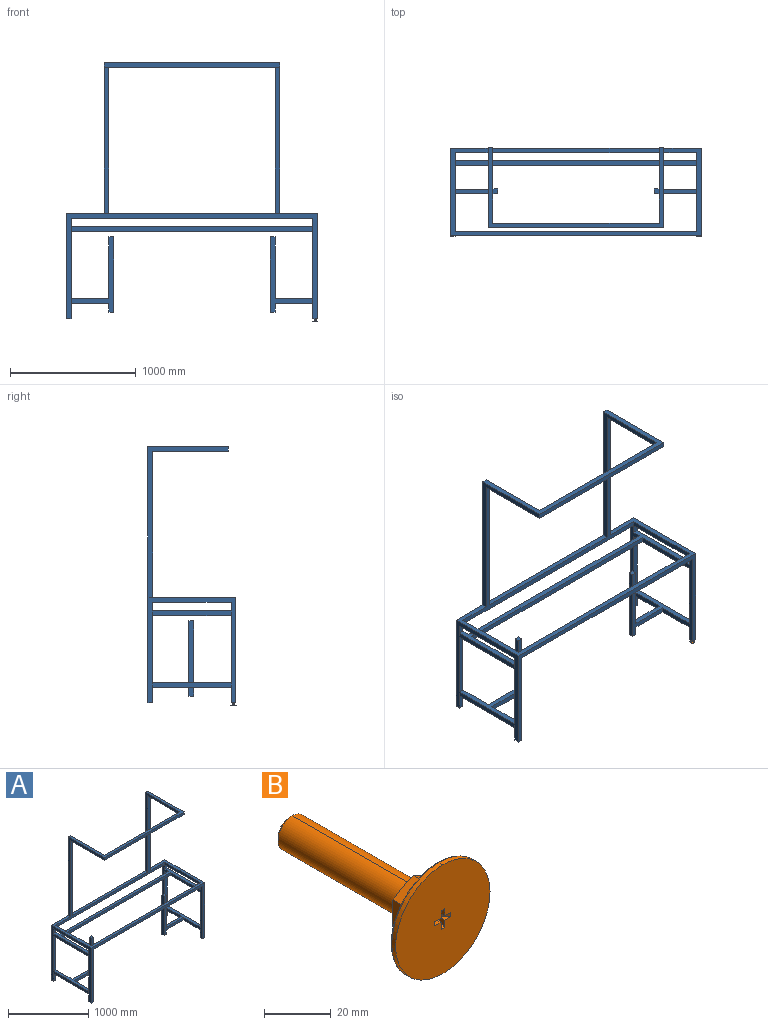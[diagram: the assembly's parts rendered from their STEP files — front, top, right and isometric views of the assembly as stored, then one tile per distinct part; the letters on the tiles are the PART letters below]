
ASSEMBLY  parts=2 mates=1
PART A: 72 faces, bbox 2000.2x700x2038.1 mm
  f0: plane 1200x600mm, normal (1,0,0), area 67128.4mm2, adj f2,f4,f19,f65,f67,f69
  f1: plane 1200x600mm, normal (-1,0,0), area 67128.4mm2, adj f2,f4,f19,f65,f67,f69
  f2: plane 1923.8x1200mm, normal (0,-1,0), area 161833.6mm2, adj f0,f1,f3,f4,f15,f21,f22,f64
  f3: plane 2000x700mm, normal (0,0,1), area 146593.6mm2, adj f2,f17,f18,f19,f20,f21,f22,f23
  f4: plane 1323.8x38.1mm, normal (0,0,1), area 50436.8mm2, adj f0,f1,f2,f19
  f5: plane 298.39x38.1mm, normal (1,0,0), area 11368.6mm2, adj f7,f51,f53,f57
  f6: plane 523.8x38.1mm, normal (1,0,0), area 19956.8mm2, adj f7,f34,f35,f39
  f7: plane 800x38.1mm, normal (0,1,0), area 27592mm2, adj f5,f6,f16,f23,f25,f26,f34,f35
  f8: plane 800x38.1mm, normal (0,-1,0), area 27592mm2, adj f16,f23,f27,f28,f34,f35,f49,f51
  f9: plane 800x325.41mm, normal (-1,0,0), area 43784.9mm2, adj f10,f12,f15,f19,f29,f31,f34,f35
  f10: plane 533.8x38.1mm, normal (0,-1,0), area 20337.8mm2, adj f9,f18,f35,f36
  f11: plane 533.8x38.1mm, normal (0,1,0), area 20337.8mm2, adj f18,f30,f35,f36
  f12: plane 70x38.1mm, normal (0,-1,0), area 2667mm2, adj f9,f14,f18,f34
  f13: plane 70x38.1mm, normal (0,1,0), area 2667mm2, adj f14,f18,f30,f34
  f14: plane 623.8x38.1mm, normal (0,0,-1), area 23766.8mm2, adj f12,f13,f18,f22
  f15: plane 1923.8x38.1mm, normal (0,0,-1), area 73296.8mm2, adj f2,f9,f19,f27
  f16: plane 623.8x38.1mm, normal (0,0,-1), area 23766.8mm2, adj f7,f8,f21,f23
  f17: plane 2000x838.1mm, normal (0,-1,0), area 137160mm2, adj f3,f18,f23,f24,f25,f26,f30,f33
  f18: plane 838.1x700mm, normal (1,0,0), area 135163.6mm2, adj f3,f10,f11,f12,f13,f14,f17,f19
  f19: plane 2038.1x2000mm, normal (0,1,0), area 228600mm2, adj f0,f1,f3,f4,f9,f15,f18,f23
  f20: plane 1923.8x38.1mm, normal (0,1,0), area 73296.8mm2, adj f3,f21,f22,f24
  f21: plane 623.8x38.1mm, normal (1,0,0), area 23766.8mm2, adj f2,f3,f16,f20
  f22: plane 623.8x38.1mm, normal (-1,0,0), area 23766.8mm2, adj f2,f3,f14,f20
  f23: plane 838.1x700mm, normal (-1,0,0), area 87630mm2, adj f3,f7,f8,f16,f17,f19,f26,f28
  f24: plane 1923.8x38.1mm, normal (0,0,-1), area 73296.8mm2, adj f17,f20,f25,f30
  f25: plane 800x38.1mm, normal (1,0,0), area 30480mm2, adj f7,f17,f24,f26
  f26: plane 38.1x38.1mm, normal (0,0,-1), area 1451.6mm2, adj f7,f17,f23,f25
  f27: plane 800x38.1mm, normal (1,0,0), area 30480mm2, adj f8,f15,f19,f28
  f28: plane 38.1x38.1mm, normal (0,0,-1), area 1451.6mm2, adj f8,f19,f23,f27
  f29: plane 120x38.1mm, normal (0,-1,0), area 4572mm2, adj f9,f18,f31,f37
  f30: plane 800x561.9mm, normal (-1,0,0), area 61805.4mm2, adj f11,f13,f17,f24,f32,f33,f34,f35
  f31: plane 38.1x38.1mm, normal (0,0,-1), area 1451.6mm2, adj f9,f18,f19,f29
  f32: plane 120x38.1mm, normal (0,1,0), area 4572mm2, adj f18,f30,f33,f37
  f33: plane 38.1x38.1mm, normal (0,0,-1), area 1415.3mm2, adj f17,f18,f30,f32,f71
  f34: plane 2000.2x623.8mm, normal (0,0,1), area 120838mm2, adj f6,f7,f8,f9,f12,f13,f18,f30
  f35: plane 2000.2x623.8mm, normal (0,0,-1), area 120838mm2, adj f6,f7,f8,f9,f10,f11,f18,f30
  f36: plane 623.8x338.1mm, normal (0,0,1), area 35196.8mm2, adj f9,f10,f11,f18,f30,f40,f41,f42
  f37: plane 623.8x338.1mm, normal (0,0,-1), area 35196.8mm2, adj f9,f18,f29,f30,f32,f40,f41,f46
  f38: plane 1924x38.1mm, normal (0,1,0), area 73304.4mm2, adj f9,f34,f35,f49
  f39: plane 1924x38.1mm, normal (0,-1,0), area 73304.4mm2, adj f6,f30,f34,f35
  f40: plane 600x338.1mm, normal (0,1,0), area 34290mm2, adj f9,f36,f37,f42,f43,f44,f45,f46
  f41: plane 600x338.1mm, normal (0,-1,0), area 34290mm2, adj f30,f36,f37,f42,f43,f44,f45,f46
  f42: plane 491.9x38.1mm, normal (1,0,0), area 18741.4mm2, adj f36,f40,f41,f43
  f43: plane 38.1x38.1mm, normal (0,0,1), area 1451.6mm2, adj f40,f41,f42,f45
  f44: plane 38.1x38.1mm, normal (0,0,-1), area 1451.6mm2, adj f40,f41,f45,f46
  f45: plane 600x38.1mm, normal (-1,0,0), area 22860mm2, adj f40,f41,f43,f44
  f46: plane 70x38.1mm, normal (1,0,0), area 2667mm2, adj f37,f40,f41,f44
  f47: plane 38.1x0.2mm, normal (0,1,0), area 7.6mm2, adj f23,f34,f35,f50
  f48: plane 38.1x0.2mm, normal (0,-1,0), area 7.6mm2, adj f23,f34,f35,f50
  f49: plane 61.9x38.1mm, normal (1,0,0), area 2358.4mm2, adj f8,f34,f35,f38
  f50: plane 623.8x38.1mm, normal (-1,0,0), area 23766.8mm2, adj f34,f35,f47,f48
  f51: plane 623.8x338.1mm, normal (0,0,1), area 35196.8mm2, adj f5,f7,f8,f52,f54,f55,f56,f57
  f52: plane 38.1x0.2mm, normal (0,1,0), area 7.6mm2, adj f23,f51,f53,f56
  f53: plane 623.8x338.1mm, normal (0,0,-1), area 35196.8mm2, adj f5,f7,f8,f52,f54,f55,f56,f57
  f54: plane 38.1x0.2mm, normal (0,-1,0), area 7.6mm2, adj f23,f51,f53,f56
  f55: plane 287.31x38.1mm, normal (1,0,0), area 10946.6mm2, adj f8,f51,f53,f58
  f56: plane 623.8x38.1mm, normal (-1,0,0), area 23766.8mm2, adj f51,f52,f53,f54
  f57: plane 600x338.1mm, normal (0,-1,0), area 34290mm2, adj f5,f51,f53,f59,f60,f61,f62,f63
  f58: plane 600x338.1mm, normal (0,1,0), area 34290mm2, adj f51,f53,f55,f59,f60,f61,f62,f63
  f59: plane 70x38.1mm, normal (-1,0,0), area 2667mm2, adj f53,f57,f58,f61
  f60: plane 38.1x38.1mm, normal (0,0,1), area 1451.6mm2, adj f57,f58,f62,f63
  f61: plane 38.1x38.1mm, normal (0,0,-1), area 1451.6mm2, adj f57,f58,f59,f62
  f62: plane 600x38.1mm, normal (1,0,0), area 22860mm2, adj f57,f58,f60,f61
  f63: plane 491.9x38.1mm, normal (-1,0,0), area 18741.4mm2, adj f51,f57,f58,f60
  f64: plane 1200x638.1mm, normal (-1,0,0), area 68580mm2, adj f2,f3,f19,f65,f67,f68
  f65: plane 1400x638.1mm, normal (0,0,1), area 99060mm2, adj f0,f1,f19,f64,f66,f68,f69
  f66: plane 1200x638.1mm, normal (1,0,0), area 68580mm2, adj f2,f3,f19,f65,f67,f68
  f67: plane 1400x600mm, normal (0,0,-1), area 96156.8mm2, adj f0,f1,f2,f64,f66,f68,f69
  f68: plane 1400x38.1mm, normal (0,-1,0), area 53340mm2, adj f64,f65,f66,f67
  f69: plane 1323.8x38.1mm, normal (0,1,0), area 50436.8mm2, adj f0,f1,f65,f67
  f70: cone r=0mm half-angle=59deg, axis (0,0,-1), area 42.4mm2, adj f71
  f71: cylinder r=3.4mm len=14.25mm, axis (0,0,-1), area 304.4mm2, adj f33,f70
PART B: 54 faces, bbox 44x65.7x44 mm
  f0: plane 9.86x9.86mm, normal (0,1,0), area 76.3mm2, adj f1,f2
  f1: cone r=4.93mm half-angle=45deg, axis (0,-1,0), area 26mm2, adj f0,f2,f4
  f2: cone r=4.93mm half-angle=45deg, axis (0,-1,0), area 26mm2, adj f0,f1,f3
  f3: cylinder r=6mm len=50.93mm, axis (0,-1,0), area 960mm2, adj f2,f4,f11
  f4: cylinder r=6mm len=50.93mm, axis (0,-1,0), area 960mm2, adj f1,f3,f11
  f5: cone r=8.5mm half-angle=75deg, axis (0,-1,0), area 3.2mm2, adj f6,f11,f17
  f6: cone r=8.5mm half-angle=75deg, axis (0,-1,0), area 3.2mm2, adj f5,f11,f16
  f7: cone r=8.5mm half-angle=75deg, axis (0,-1,0), area 6.4mm2, adj f11,f15,f16
  f8: cone r=8.5mm half-angle=75deg, axis (0,-1,0), area 6.4mm2, adj f11,f14,f19
  f9: cone r=8.5mm half-angle=75deg, axis (0,-1,0), area 6.4mm2, adj f11,f18,f19
  f10: cone r=8.5mm half-angle=75deg, axis (0,-1,0), area 6.4mm2, adj f11,f17,f18
  f11: plane 17x17mm, normal (0,1,0), area 113.9mm2, adj f3,f4,f5,f6,f7,f8,f9,f10
  f12: cone r=8.5mm half-angle=75deg, axis (0,-1,0), area 6.4mm2, adj f11,f14,f15
  f13: cone r=8.49mm half-angle=60deg, axis (0,-1,0), area 563mm2, adj f14,f15,f16,f20,f53
  f14: plane 9.23x5.9mm, normal (-0.5,0,0.87), area 44.7mm2, adj f8,f12,f13,f15,f19
  f15: plane 10.55x5.9mm, normal (-1,0,0), area 44.7mm2, adj f7,f12,f13,f14,f16
  f16: plane 9.23x5.9mm, normal (-0.5,0,-0.87), area 44.7mm2, adj f6,f7,f13,f15,f17
  f17: plane 9.23x5.9mm, normal (0.5,0,-0.87), area 44.7mm2, adj f5,f10,f16,f18,f20
  f18: plane 10.55x5.9mm, normal (1,0,0), area 44.7mm2, adj f9,f10,f17,f19,f20
  f19: plane 9.23x5.9mm, normal (0.5,0,0.87), area 44.7mm2, adj f8,f9,f14,f18,f20
  f20: cone r=8.49mm half-angle=60deg, axis (0,-1,0), area 563mm2, adj f13,f17,f18,f19,f21
  f21: torus R=19.5mm, axis (0,1,0), area 32.8mm2, adj f20,f51,f53
  f22: plane 1.5x0.51mm, normal (1,0,0), area 0.5mm2, adj f23,f37,f38,f46
  f23: plane 0.25x0.21mm, normal (0,-0.64,0.77), area 0mm2, adj f22,f24,f37
  f24: plane 0.25x0.21mm, normal (0.77,-0.64,0), area 0mm2, adj f23,f25,f36
  f25: plane 1.5x0.51mm, normal (0,0,1), area 0.5mm2, adj f24,f26,f36,f49
  f26: plane 0.25x0.21mm, normal (-0.77,-0.64,0), area 0mm2, adj f25,f27,f36
  f27: plane 0.25x0.21mm, normal (0,-0.64,0.77), area 0mm2, adj f26,f33,f35
  f28: plane 3.2x2.68mm, normal (-1,0,0), area 4.3mm2, adj f29,f49,f50
  f29: plane 3.2x2.68mm, normal (0,0,1), area 4.3mm2, adj f28,f32,f50
  f30: plane 3.2x2.68mm, normal (-1,0,0), area 4.3mm2, adj f31,f43,f50
  f31: plane 3.2x2.68mm, normal (0,0,-1), area 4.3mm2, adj f30,f32,f50
  f32: plane 3.2x2.68mm, normal (-0.77,-0.64,0), area 6.3mm2, adj f29,f31,f33,f50
  f33: plane 1.5x0.51mm, normal (-1,0,0), area 0.5mm2, adj f27,f32,f34,f35
  f34: plane 0.25x0.21mm, normal (0,-0.64,-0.77), area 0mm2, adj f33,f35,f41
  f35: cylinder r=0.7mm len=1.07mm, axis (-1,0,0), area 0.6mm2, adj f27,f33,f34,f36,f40
  f36: cylinder r=0.7mm len=1.07mm, axis (0,0,-1), area 0.6mm2, adj f24,f25,f26,f35,f37
  f37: cylinder r=0.7mm len=1.07mm, axis (-1,0,0), area 0.6mm2, adj f22,f23,f36,f38,f40
  f38: plane 0.25x0.21mm, normal (0,-0.64,-0.77), area 0mm2, adj f22,f37,f39
  f39: plane 0.25x0.21mm, normal (0.77,-0.64,0), area 0mm2, adj f38,f40,f42
  f40: cylinder r=0.7mm len=1.07mm, axis (0,0,-1), area 0.6mm2, adj f35,f37,f39,f41,f42
  f41: plane 0.25x0.21mm, normal (-0.77,-0.64,0), area 0mm2, adj f34,f40,f42
  f42: plane 1.5x0.51mm, normal (0,0,-1), area 0.5mm2, adj f39,f40,f41,f43
  f43: plane 3.2x2.68mm, normal (0,-0.64,-0.77), area 6.3mm2, adj f30,f42,f44,f50
  f44: plane 3.2x2.68mm, normal (1,0,0), area 4.3mm2, adj f43,f45,f50
  f45: plane 3.2x2.68mm, normal (0,0,-1), area 4.3mm2, adj f44,f46,f50
  f46: plane 3.2x2.68mm, normal (0.77,-0.64,0), area 6.3mm2, adj f22,f45,f47,f50
  f47: plane 3.2x2.68mm, normal (0,0,1), area 4.3mm2, adj f46,f48,f50
  f48: plane 3.2x2.68mm, normal (1,0,0), area 4.3mm2, adj f47,f49,f50
  f49: plane 3.2x2.68mm, normal (0,-0.64,0.77), area 6.3mm2, adj f25,f28,f48,f50
  f50: plane 40x40mm, normal (0,-1,0), area 1238.3mm2, adj f28,f29,f30,f31,f32,f43,f44,f45
  f51: cylinder r=20mm len=40mm, axis (0,-1,0), area 104.4mm2, adj f21,f50,f52
  f52: cylinder r=20mm len=40mm, axis (0,-1,0), area 104.4mm2, adj f50,f51,f53
  f53: torus R=19.5mm, axis (0,1,0), area 32.8mm2, adj f13,f21,f52
PLACE A t=(25.99,36.06,80.33)mm fixed
PLACE B rot(axis=(1,0,0),90deg) t=(1006.94,-294.89,-780.77)mm
MATE fastened B.f1 <-> A.f70  axis (0,0,1) through (1006.94,-294.89,-767.77)mm
